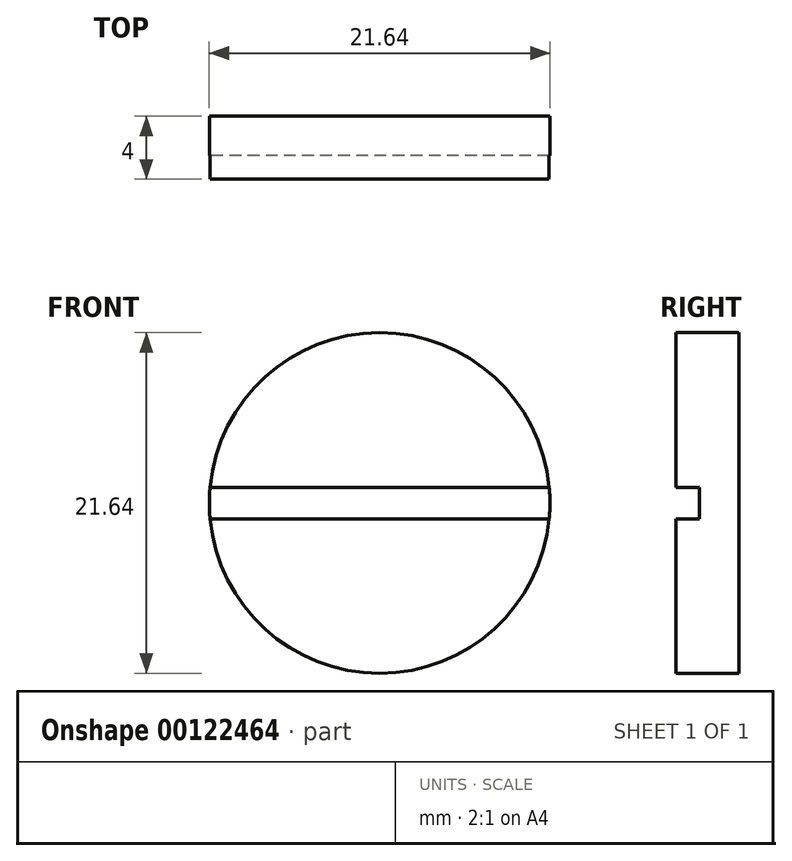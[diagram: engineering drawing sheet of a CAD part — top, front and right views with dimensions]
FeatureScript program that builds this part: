
annotation { "Feature Type Name" : "Feature", "Feature Type Description" : "" }
export const myFeature = defineFeature(function(context is Context, id is Id, definition is map)
    precondition{}
    {
        {
            var Q0;
            Q0=qCreatedBy(makeId("Front.planeOp"),FACE);
            var sketch = newSketch(context, id + "F0", { "sketchPlane" : qUnion([Q0])});
            skCircle(sketch, "E0", {"center": v(0, 0) * mm, "radius": 10.81 * mm});
            skSolve(sketch);
        }
        {
            var Q0;
            Q0 = qSketchRegion(id + "F0", true);
            extrude(context, id + "F1", {"entities" : qUnion([Q0]), "oppositeDirection" : true, "depth" : 4 * mm});
        }
        {
            var Q0;
            Q0=qCreatedBy(makeId("Right.planeOp"),FACE);
            var sketch = newSketch(context, id + "F2", { "sketchPlane" : qUnion([Q0])});
            skLineSegment(sketch, "E1", {"start": v(0, -1) * mm, "end": v(0, 1) * mm});
            skLineSegment(sketch, "E2", {"start": v(0, 1) * mm, "end": v(1.5, 1) * mm});
            skLineSegment(sketch, "E3", {"start": v(1.5, 1) * mm, "end": v(1.5, -1) * mm});
            skLineSegment(sketch, "E4", {"start": v(1.5, -1) * mm, "end": v(0, -1) * mm});
            skSolve(sketch);
        }
        {
            var Q0;
            Q0 = qSketchRegion(id + "F2", true);
            extrude(context, id + "F3", {"entities" : qUnion([Q0]), "operationType" : NewBodyOperationType.REMOVE, "endBound" : BoundingType.SYMMETRIC, "depth" : 25 * mm});
        }
    });
